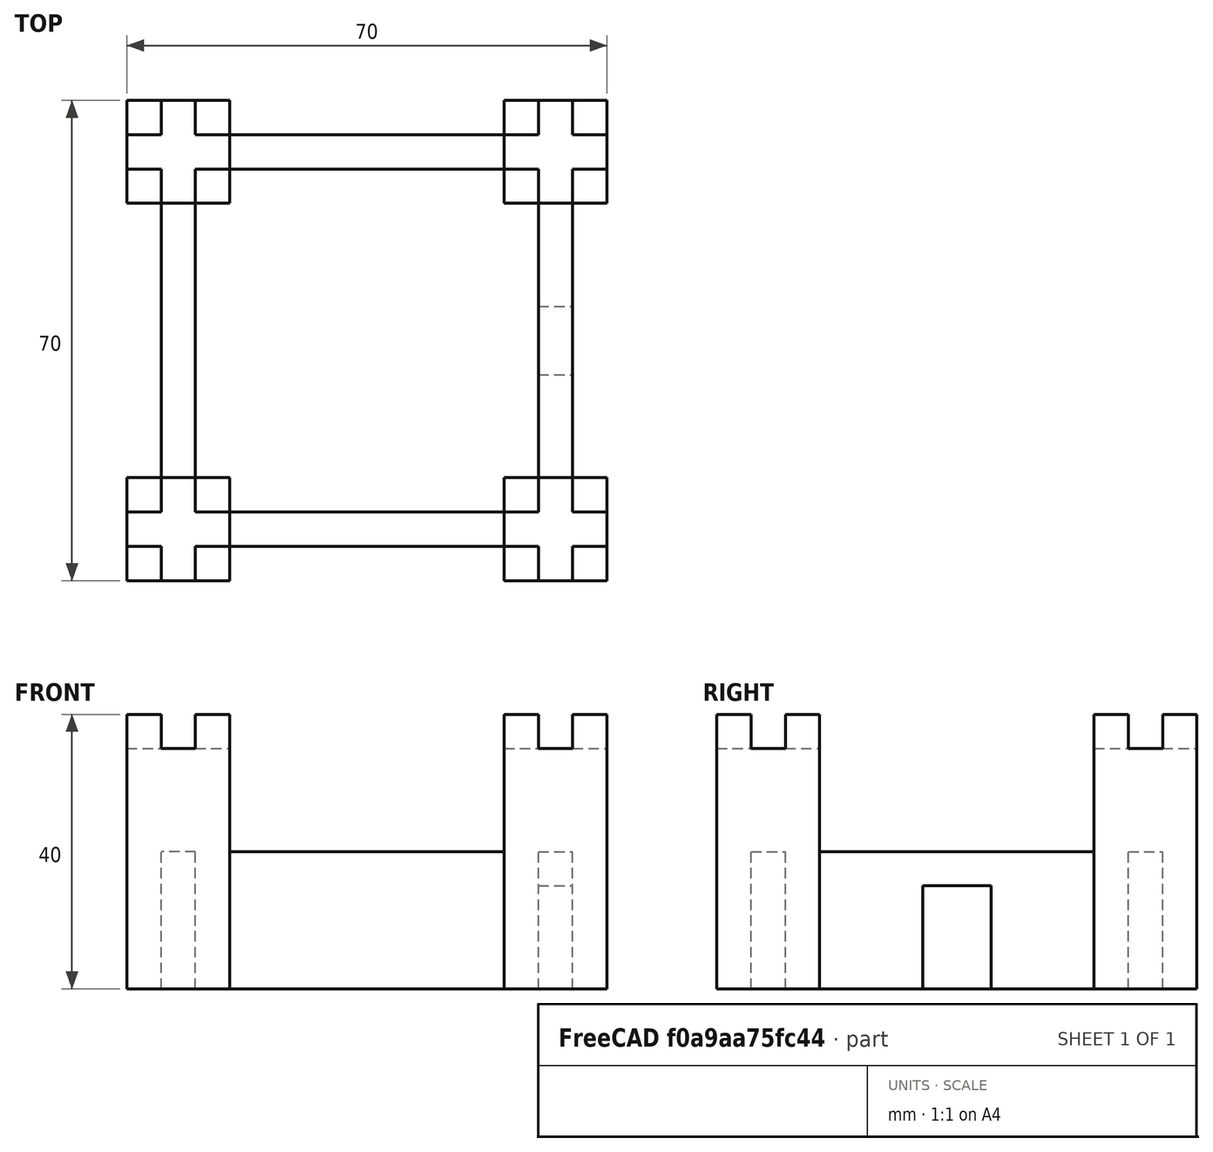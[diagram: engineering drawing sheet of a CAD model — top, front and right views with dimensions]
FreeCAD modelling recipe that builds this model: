
FCSTD DOCUMENT  (FreeCAD 0.20R29410 (Git))
Label: castillo
License: Creative Commons Attribution
LicenseURL: http://creativecommons.org/licenses/by/4.0/
objects: Part::Box×29, Part::Cut×21
note: 50 computed .brp shape members not serialized (recipe doc carries the construction recipe); baked Part::Feature solids carry a one-line shape summary decoded from their .brp

FEATURE [Part::Box] Box  label="Cubo"
  AttacherType = Attacher::AttachEngine3D
  Height = 40
  Length = 15
  Width = 15
FEATURE [Part::Box] Box001  label="Cubo001"
  AttacherType = Attacher::AttachEngine3D
  Height = 5
  Length = 5
  Placement = pos=(5,0,35) rot=(0,0,1;0rad)
  Width = 5
FEATURE [Part::Box] Box002  label="Cubo002"
  AttacherType = Attacher::AttachEngine3D
  Height = 5
  Length = 5
  Placement = pos=(0,5,35) rot=(0,0,1;0rad)
  Width = 5
FEATURE [Part::Box] Box003  label="Cubo003"
  AttacherType = Attacher::AttachEngine3D
  Height = 5
  Length = 5
  Placement = pos=(10,5,35) rot=(0,0,1;0rad)
  Width = 5
FEATURE [Part::Box] Box004  label="Cubo004"
  AttacherType = Attacher::AttachEngine3D
  Height = 5
  Length = 5
  Placement = pos=(5,10,35) rot=(0,0,1;0rad)
  Width = 5
FEATURE [Part::Cut] Cut
  Base = -> Box
  Refine = true
  Tool = -> Box001
FEATURE [Part::Cut] Cut001
  Base = -> Cut
  Refine = true
  Tool = -> Box002
FEATURE [Part::Cut] Cut002
  Base = -> Cut001
  Refine = true
  Tool = -> Box004
FEATURE [Part::Box] Box005  label="Cubo005"
  AttacherType = Attacher::AttachEngine3D
  Height = 5
  Length = 5
  Placement = pos=(5,5,35) rot=(0,0,1;0rad)
  Width = 5
FEATURE [Part::Cut] Cut003
  Base = -> Cut002
  Refine = true
  Tool = -> Box005
FEATURE [Part::Cut] Cut004  label="torre1"
  Base = -> Cut003
  Refine = true
  Tool = -> Box003
FEATURE [Part::Box] Box006  label="puerta"
  AttacherType = Attacher::AttachEngine3D
  Height = 20
  Length = 5
  Placement = pos=(5,15,0) rot=(0,0,1;0rad)
  Width = 40
FEATURE [Part::Box] Box007  label="Cubo006"
  AttacherType = Attacher::AttachEngine3D
  Height = 15
  Length = 5
  Placement = pos=(5,30,0) rot=(0,0,1;0rad)
  Width = 10
FEATURE [Part::Cut] Cut005  label="puertaa"
  Base = -> Box006
  Refine = true
  Tool = -> Box007
FEATURE [Part::Box] Box008  label="Cubo007"
  AttacherType = Attacher::AttachEngine3D
  Height = 40
  Length = 15
  Width = 15
FEATURE [Part::Box] Box009  label="Cubo008"
  AttacherType = Attacher::AttachEngine3D
  Height = 5
  Length = 5
  Placement = pos=(5,0,35) rot=(0,0,1;0rad)
  Width = 5
FEATURE [Part::Box] Box010  label="Cubo009"
  AttacherType = Attacher::AttachEngine3D
  Height = 5
  Length = 5
  Placement = pos=(0,5,35) rot=(0,0,1;0rad)
  Width = 5
FEATURE [Part::Box] Box011  label="Cubo010"
  AttacherType = Attacher::AttachEngine3D
  Height = 5
  Length = 5
  Placement = pos=(10,5,35) rot=(0,0,1;0rad)
  Width = 5
FEATURE [Part::Box] Box012  label="Cubo011"
  AttacherType = Attacher::AttachEngine3D
  Height = 5
  Length = 5
  Placement = pos=(5,10,35) rot=(0,0,1;0rad)
  Width = 5
FEATURE [Part::Box] Box013  label="Cubo012"
  AttacherType = Attacher::AttachEngine3D
  Height = 5
  Length = 5
  Placement = pos=(5,5,35) rot=(0,0,1;0rad)
  Width = 5
FEATURE [Part::Cut] Cut006
  Base = -> Box008
  Refine = true
  Tool = -> Box009
FEATURE [Part::Cut] Cut007
  Base = -> Cut006
  Refine = true
  Tool = -> Box010
FEATURE [Part::Cut] Cut008
  Base = -> Cut007
  Refine = true
  Tool = -> Box012
FEATURE [Part::Cut] Cut009
  Base = -> Cut008
  Refine = true
  Tool = -> Box013
FEATURE [Part::Cut] Cut010  label="torre002"
  Base = -> Cut009
  Placement = pos=(0,55,0) rot=(0,0,1;0rad)
  Refine = true
  Tool = -> Box011
FEATURE [Part::Box] Box014  label="pared1"
  AttacherType = Attacher::AttachEngine3D
  Height = 20
  Length = 5
  Placement = pos=(3.8e-15,60,0) rot=(0,0,1;1.5708rad)
  Width = 40
FEATURE [Part::Box] Box015  label="Cubo014"
  AttacherType = Attacher::AttachEngine3D
  Height = 40
  Length = 15
  Width = 15
FEATURE [Part::Box] Box016  label="Cubo015"
  AttacherType = Attacher::AttachEngine3D
  Height = 5
  Length = 5
  Placement = pos=(5,0,35) rot=(0,0,1;0rad)
  Width = 5
FEATURE [Part::Box] Box017  label="Cubo016"
  AttacherType = Attacher::AttachEngine3D
  Height = 5
  Length = 5
  Placement = pos=(0,5,35) rot=(0,0,1;0rad)
  Width = 5
FEATURE [Part::Box] Box018  label="Cubo017"
  AttacherType = Attacher::AttachEngine3D
  Height = 5
  Length = 5
  Placement = pos=(10,5,35) rot=(0,0,1;0rad)
  Width = 5
FEATURE [Part::Box] Box019  label="Cubo018"
  AttacherType = Attacher::AttachEngine3D
  Height = 5
  Length = 5
  Placement = pos=(5,10,35) rot=(0,0,1;0rad)
  Width = 5
FEATURE [Part::Box] Box020  label="Cubo019"
  AttacherType = Attacher::AttachEngine3D
  Height = 5
  Length = 5
  Placement = pos=(5,5,35) rot=(0,0,1;0rad)
  Width = 5
FEATURE [Part::Cut] Cut011
  Base = -> Box015
  Refine = true
  Tool = -> Box016
FEATURE [Part::Cut] Cut012
  Base = -> Cut011
  Refine = true
  Tool = -> Box017
FEATURE [Part::Cut] Cut013
  Base = -> Cut012
  Refine = true
  Tool = -> Box019
FEATURE [Part::Cut] Cut014
  Base = -> Cut013
  Refine = true
  Tool = -> Box020
FEATURE [Part::Cut] Cut015  label="torre003"
  Base = -> Cut014
  Placement = pos=(-55,55,0) rot=(0,0,1;0rad)
  Refine = true
  Tool = -> Box018
FEATURE [Part::Box] Box021  label="pared002"
  AttacherType = Attacher::AttachEngine3D
  Height = 20
  Length = 5
  Placement = pos=(-45,55,0) rot=(0,0,1;3.14159rad)
  Width = 40
FEATURE [Part::Box] Box022  label="Cubo020"
  AttacherType = Attacher::AttachEngine3D
  Height = 40
  Length = 15
  Width = 15
FEATURE [Part::Box] Box023  label="Cubo021"
  AttacherType = Attacher::AttachEngine3D
  Height = 5
  Length = 5
  Placement = pos=(5,0,35) rot=(0,0,1;0rad)
  Width = 5
FEATURE [Part::Box] Box024  label="Cubo022"
  AttacherType = Attacher::AttachEngine3D
  Height = 5
  Length = 5
  Placement = pos=(0,5,35) rot=(0,0,1;0rad)
  Width = 5
FEATURE [Part::Box] Box025  label="Cubo023"
  AttacherType = Attacher::AttachEngine3D
  Height = 5
  Length = 5
  Placement = pos=(10,5,35) rot=(0,0,1;0rad)
  Width = 5
FEATURE [Part::Box] Box026  label="Cubo024"
  AttacherType = Attacher::AttachEngine3D
  Height = 5
  Length = 5
  Placement = pos=(5,10,35) rot=(0,0,1;0rad)
  Width = 5
FEATURE [Part::Box] Box027  label="Cubo025"
  AttacherType = Attacher::AttachEngine3D
  Height = 5
  Length = 5
  Placement = pos=(5,5,35) rot=(0,0,1;0rad)
  Width = 5
FEATURE [Part::Cut] Cut016
  Base = -> Box022
  Refine = true
  Tool = -> Box023
FEATURE [Part::Cut] Cut017
  Base = -> Cut016
  Refine = true
  Tool = -> Box024
FEATURE [Part::Cut] Cut018
  Base = -> Cut017
  Refine = true
  Tool = -> Box026
FEATURE [Part::Cut] Cut019
  Base = -> Cut018
  Refine = true
  Tool = -> Box027
FEATURE [Part::Cut] Cut020  label="torre004"
  Base = -> Cut019
  Placement = pos=(-55,0,0) rot=(0,0,1;0rad)
  Refine = true
  Tool = -> Box025
FEATURE [Part::Box] Box028  label="pared003"
  AttacherType = Attacher::AttachEngine3D
  Height = 20
  Length = 5
  Placement = pos=(-8.2e-15,5,0) rot=(0,0,1;1.5708rad)
  Width = 40
